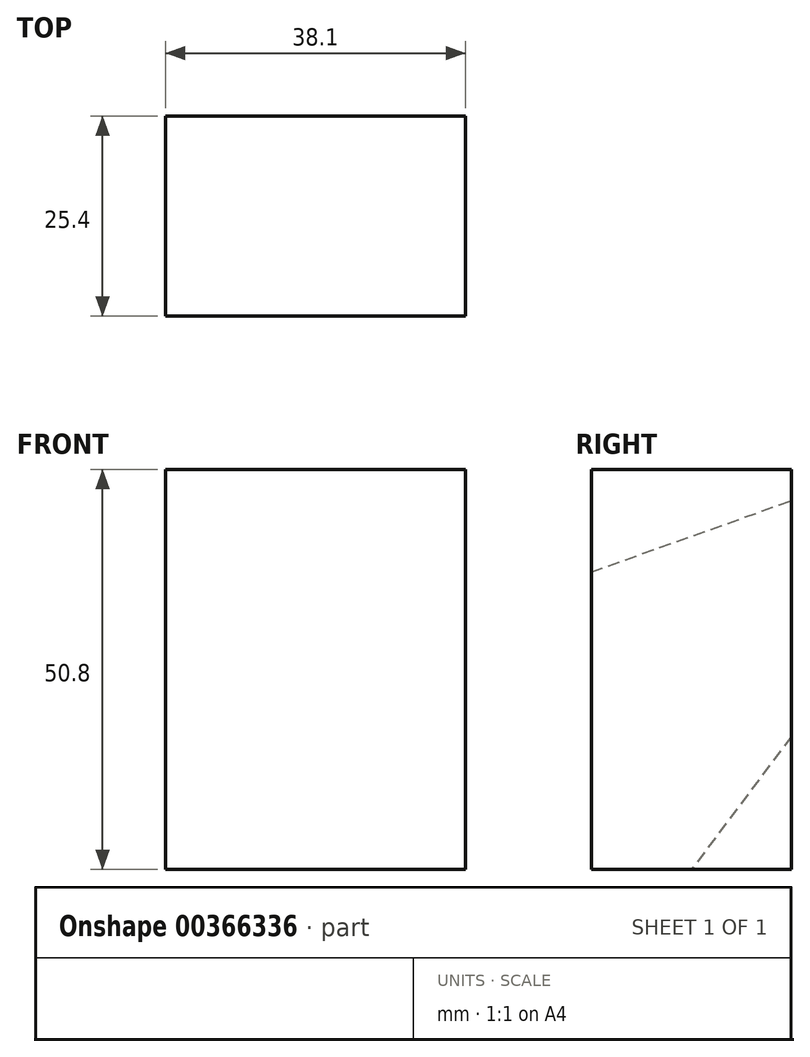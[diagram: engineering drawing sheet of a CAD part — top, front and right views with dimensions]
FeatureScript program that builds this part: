
annotation { "Feature Type Name" : "Feature", "Feature Type Description" : "" }
export const myFeature = defineFeature(function(context is Context, id is Id, definition is map)
    precondition{}
    {
        {
            var Q0;
            Q0=qCreatedBy(makeId("Front.planeOp"),FACE);
            var sketch = newSketch(context, id + "F0", { "sketchPlane" : qUnion([Q0])});
            skLineSegment(sketch, "E0", {"start": v(0, 50.8) * mm, "end": v(0, 0) * mm});
            skLineSegment(sketch, "E1", {"start": v(0, 50.8) * mm, "end": v(38.1, 50.8) * mm});
            skLineSegment(sketch, "E2", {"start": v(38.1, 50.8) * mm, "end": v(38.1, 0) * mm});
            skLineSegment(sketch, "E3", {"start": v(38.1, 0) * mm, "end": v(0, 0) * mm});
            skSolve(sketch);
        }
        {
            var Q0;
            Q0 = qSketchRegion(id + "F0", true);
            extrude(context, id + "F1", {"entities" : qUnion([Q0]), "depth" : 25.4 * mm});
        }
        {
            var Q0;
            Q0=makeQuery(id+"F1.opExtrude","SWEPT_FACE",FACE,{"disambiguationData":[OSD([sQuery(id+"F0.wireOp",EDGE,"E0")])]});
            var sketch = newSketch(context, id + "F2", { "sketchPlane" : qUnion([Q0])});
            skLineSegment(sketch, "E4", {"start": v(25.4, 37.8) * mm, "end": v(0, 46.84) * mm});
            skLineSegment(sketch, "E5", {"start": v(0, 46.84) * mm, "end": v(0, 16.89) * mm});
            skLineSegment(sketch, "E6", {"start": v(0, 16.89) * mm, "end": v(12.7, 0) * mm});
            skLineSegment(sketch, "E7", {"start": v(12.7, 0) * mm, "end": v(25.4, 0) * mm});
            skLineSegment(sketch, "E8", {"start": v(25.4, 0) * mm, "end": v(25.4, 37.8) * mm});
            skSolve(sketch);
        }
        {
            var Q0;
            Q0=makeQuery(id+"F2.imprint","IMPRINT",FACE,{"disambiguationData":[TD([[makeQuery(id+"F2.imprint","IMPRINT",EDGE,{"derivedFrom":sQuery(id+"F2.wireOp",EDGE,"E4")}),1.0]])]});
            extrude(context, id + "F3", {"entities" : qUnion([Q0]), "operationType" : NewBodyOperationType.REMOVE, "oppositeDirection" : true, "depth" : 2 / 101.6 * mm});
        }
    });
